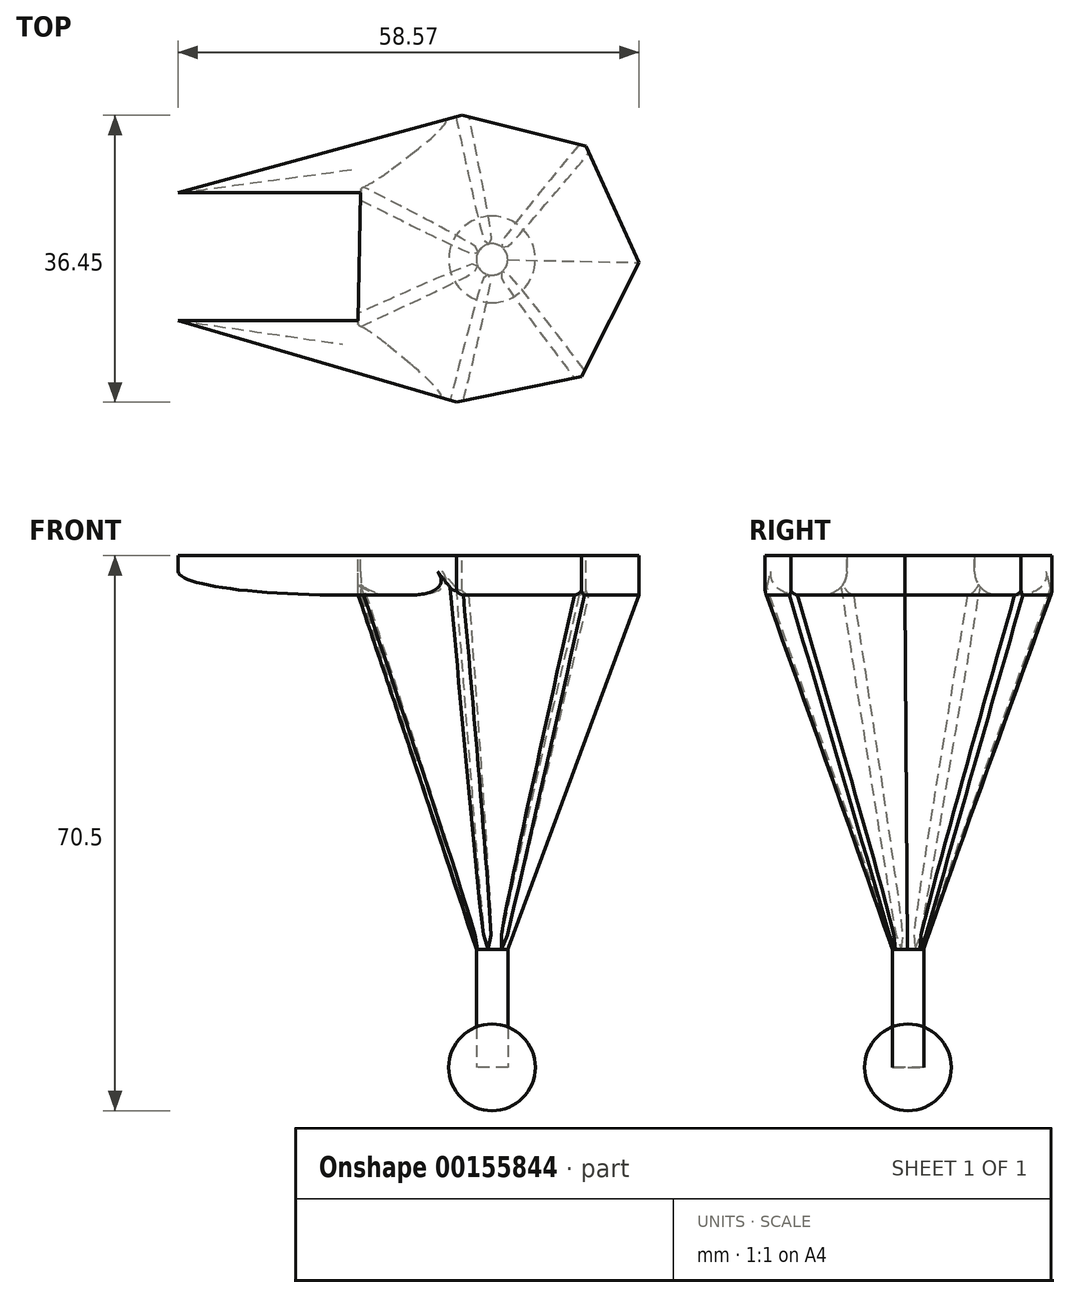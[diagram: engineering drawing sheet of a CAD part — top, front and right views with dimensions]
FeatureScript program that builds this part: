
annotation { "Feature Type Name" : "Feature", "Feature Type Description" : "" }
export const myFeature = defineFeature(function(context is Context, id is Id, definition is map)
    precondition{}
    {
        {
            var Q0;
            Q0=qCreatedBy(makeId("Top.planeOp"),FACE);
            var sketch = newSketch(context, id + "F0", { "sketchPlane" : qUnion([Q0])});
            skArc(sketch, "E0", {"start": v(-48.64, 0.62) * mm, "mid": v(-54.14, -4.88) * mm, "end": v(-48.64, -10.38) * mm});
            skLineSegment(sketch, "E1", {"start": v(-48.64, 0.62) * mm, "end": v(-48.64, -10.38) * mm});
            skSolve(sketch);
        }
        {
            var Q0;
            Q0=makeQuery(id+"F0.imprint","IMPRINT",FACE,{"disambiguationData":[TD([[makeQuery(id+"F0.imprint","IMPRINT",EDGE,{"derivedFrom":sQuery(id+"F0.wireOp",EDGE,"E0")}),1.0]])]});
            var Q1;
            Q1=sQuery(id+"F0.wireOp",EDGE,"E1");
            revolve(context, id + "F1", {"entities" : qUnion([Q0]), "axis" : qUnion([Q1]), "revolveType" : RevolveType.FULL});
        }
        {
            var Q0;
            Q0=qCreatedBy(makeId("Top.planeOp"),FACE);
            var sketch = newSketch(context, id + "F2", { "sketchPlane" : qUnion([Q0])});
            skPoint(sketch, "E2.0", {"position": v(-48.64, -4.88) * mm});
            skCircle(sketch, "E3", {"center": v(-48.64, -4.88) * mm, "radius": 2 * mm});
            skSolve(sketch);
        }
        {
            var Q0;
            Q0=makeQuery(id+"F2.imprint","IMPRINT",FACE,{"disambiguationData":[TD([[makeQuery(id+"F2.imprint","IMPRINT",EDGE,{"derivedFrom":sQuery(id+"F2.wireOp",EDGE,"E3")}),1.0]])]});
            extrude(context, id + "F3", {"entities" : qUnion([Q0]), "depth" : 15 * mm});
        }
        {
            var Q0;
            Q0=qCreatedBy(makeId("Top.planeOp"),FACE);
            cPlane(context, id + "F4", {"entities" : qUnion([Q0]), "cplaneType" : CPlaneType.OFFSET, "offset" : 60 * mm, "width" : 150 * mm, "height" : 150 * mm});
        }
        {
            var Q0;
            Q0=qCreatedBy(id+"F4.planeOp",FACE);
            var sketch = newSketch(context, id + "F5", { "sketchPlane" : qUnion([Q0])});
            skPoint(sketch, "E4.0", {"position": v(-48.64, -4.88) * mm});
            skCircle(sketch, "E5.cCircle", {"center": v(-48.64, -4.88) * mm, "radius": 16.84 * mm, "construction": true});
            skLineSegment(sketch, "E5.0", {"start": v(-37.3, -19.74) * mm, "end": v(-53.18, -23.02) * mm});
            skLineSegment(sketch, "E5.1", {"start": v(-53.18, -23.02) * mm, "end": v(-65.65, -12.64) * mm});
            skLineSegment(sketch, "E5.2", {"start": v(-65.65, -12.64) * mm, "end": v(-65.32, 3.58) * mm});
            skLineSegment(sketch, "E5.3", {"start": v(-65.32, 3.58) * mm, "end": v(-52.43, 13.43) * mm});
            skLineSegment(sketch, "E5.4", {"start": v(-52.43, 13.43) * mm, "end": v(-36.69, 9.5) * mm});
            skLineSegment(sketch, "E5.5", {"start": v(-36.69, 9.5) * mm, "end": v(-29.95, -5.27) * mm});
            skLineSegment(sketch, "E5.6", {"start": v(-29.95, -5.27) * mm, "end": v(-37.3, -19.74) * mm});
            skPoint(sketch, "E5.0.midPoint", {"position": v(-45.24, -21.38) * mm});
            skSolve(sketch);
        }
        {
            var Q0;
            Q0=makeQuery(id+"F3.opExtrude","CAP_FACE",FACE,{"disambiguationData":[OSD([sQuery(id+"F2.wireOp",EDGE,"E3")])],"isStart":false});
            var Q1;
            Q1=makeQuery(id+"F5.imprint","IMPRINT",FACE,{"disambiguationData":[TD([[makeQuery(id+"F5.imprint","IMPRINT",EDGE,{"derivedFrom":sQuery(id+"F5.wireOp",EDGE,"E5.0")}),-1.0]])]});
            loft(context, id + "F6", {"sheetProfilesArray" : [{ "sheetProfileEntities" : qUnion([Q0]) }, { "sheetProfileEntities" : qUnion([Q1]) }]});
        }
        {
            var Q0;
            Q0=makeQuery(id+"F6.opLoft","CAP_FACE",FACE,{"disambiguationData":[OSD([makeQuery(id+"F5.imprint","IMPRINT",FACE,{"disambiguationData":[TD([[makeQuery(id+"F5.imprint","IMPRINT",EDGE,{"derivedFrom":sQuery(id+"F5.wireOp",EDGE,"E5.0")}),-1.0]])]})])],"isStart":true});
            var sketch = newSketch(context, id + "F7", { "sketchPlane" : qUnion([Q0])});
            skLineSegment(sketch, "E6", {"start": v(-52.43, 13.43) * mm, "end": v(-88.52, 3.58) * mm});
            skLineSegment(sketch, "E7", {"start": v(-53.18, -23.02) * mm, "end": v(-88.52, -12.64) * mm});
            skLineSegment(sketch, "E8", {"start": v(-88.52, -12.64) * mm, "end": v(-65.65, -12.64) * mm});
            skLineSegment(sketch, "E9", {"start": v(-88.52, 3.58) * mm, "end": v(-65.32, 3.58) * mm});
            skSolve(sketch);
        }
        {
            var Q0;
            Q0=makeQuery(id+"F7.imprint","IMPRINT",FACE,{"disambiguationData":[TD([[makeQuery(id+"F7.imprint","IMPRINT",EDGE,{"derivedFrom":sQuery(id+"F7.wireOp",EDGE,"E6")}),1.0]])]});
            var Q1;
            {var subQ2=sQuery(id+"F5.wireOp",EDGE,"E5.1");var subQ3=sQuery(id+"F5.wireOp",EDGE,"E5.0");var subQ4=sQuery(id+"F5.wireOp",EDGE,"E5.6");Q1=makeQuery(id+"F7.imprint","IMPRINT",FACE,{"disambiguationData":[TD([[makeQuery(id+"F7.imprint","IMPRINT",EDGE,{"derivedFrom":makeQuery(id+"F6.opLoft","MID_CAP_EDGE",EDGE,{"disambiguationData":[OSD([subQ3,subQ2,subQ4])],"capPos":1.0})}),1.0]])]});}
            var Q2;
            Q2=makeQuery(id+"F7.imprint","IMPRINT",FACE,{"disambiguationData":[TD([[makeQuery(id+"F7.imprint","IMPRINT",EDGE,{"derivedFrom":sQuery(id+"F7.wireOp",EDGE,"E7")}),-1.0]])]});
            extrude(context, id + "F8", {"entities" : qUnion([Q0, Q1, Q2]), "operationType" : NewBodyOperationType.ADD, "depth" : 5 * mm});
        }
        {
            var Q0;
            Q0=makeQuery(id+"F8.opExtrude","CAP_EDGE",EDGE,{"disambiguationData":[OSD([sQuery(id+"F7.wireOp",EDGE,"E7")])],"isStart":true});
            var Q1;
            Q1=makeQuery(id+"F8.opExtrude","CAP_EDGE",EDGE,{"disambiguationData":[OSD([sQuery(id+"F7.wireOp",EDGE,"E8")])],"isStart":true});
            var Q2;
            Q2=makeQuery(id+"F8.opExtrude","CAP_EDGE",EDGE,{"disambiguationData":[OSD([sQuery(id+"F7.wireOp",EDGE,"E9")])],"isStart":true});
            var Q3;
            Q3=makeQuery(id+"F8.opExtrude","CAP_EDGE",EDGE,{"disambiguationData":[OSD([sQuery(id+"F7.wireOp",EDGE,"E6")])],"isStart":true});
            fillet(context, id + "F9", {"entities" : qUnion([Q0, Q1, Q2, Q3]), "radius" : 3 * mm, "tangentPropagation" : true, "allowEdgeOverflow" : false});
        }
        {
            var Q0;
            Q0=makeQuery(id+"F6.opLoft","SWEPT_EDGE",EDGE,{"disambiguationData":[OSD([sQuery(id+"F2.wireOp",EDGE,"E3"),sQuery(id+"F5.wireOp",EDGE,"E5.1"),sQuery(id+"F5.wireOp",EDGE,"E5.2"),sQuery(id+"F5.wireOp",EDGE,"E5.3")])]});
            var Q1;
            Q1=makeQuery(id+"F6.opLoft","SWEPT_EDGE",EDGE,{"disambiguationData":[OSD([sQuery(id+"F2.wireOp",EDGE,"E3"),sQuery(id+"F5.wireOp",EDGE,"E5.2"),sQuery(id+"F5.wireOp",EDGE,"E5.3"),sQuery(id+"F5.wireOp",EDGE,"E5.4")])]});
            var Q2;
            Q2=makeQuery(id+"F6.opLoft","SWEPT_EDGE",EDGE,{"disambiguationData":[OSD([sQuery(id+"F2.wireOp",EDGE,"E3"),sQuery(id+"F5.wireOp",EDGE,"E5.0"),sQuery(id+"F5.wireOp",EDGE,"E5.1"),sQuery(id+"F5.wireOp",EDGE,"E5.2")])]});
            var Q3;
            Q3=makeQuery(id+"F6.opLoft","SWEPT_EDGE",EDGE,{"disambiguationData":[OSD([sQuery(id+"F5.wireOp",EDGE,"E5.0"),sQuery(id+"F5.wireOp",EDGE,"E5.6")])]});
            var Q4;
            Q4=makeQuery(id+"F6.opLoft","SWEPT_EDGE",EDGE,{"disambiguationData":[OSD([sQuery(id+"F2.wireOp",EDGE,"E3"),sQuery(id+"F5.wireOp",EDGE,"E5.3"),sQuery(id+"F5.wireOp",EDGE,"E5.4"),sQuery(id+"F5.wireOp",EDGE,"E5.5")])]});
            var Q5;
            Q5=makeQuery(id+"F6.opLoft","SWEPT_EDGE",EDGE,{"disambiguationData":[OSD([sQuery(id+"F2.wireOp",EDGE,"E3"),sQuery(id+"F5.wireOp",EDGE,"E5.4"),sQuery(id+"F5.wireOp",EDGE,"E5.5"),sQuery(id+"F5.wireOp",EDGE,"E5.6")])]});
            var Q6;
            Q6=makeQuery(id+"F6.opLoft","SWEPT_EDGE",EDGE,{"disambiguationData":[OSD([sQuery(id+"F2.wireOp",EDGE,"E3"),sQuery(id+"F5.wireOp",EDGE,"E5.0"),sQuery(id+"F5.wireOp",EDGE,"E5.5"),sQuery(id+"F5.wireOp",EDGE,"E5.6")])]});
            fillet(context, id + "F10", {"entities" : qUnion([Q0, Q1, Q2, Q3, Q4, Q5, Q6]), "radius" : 2 * mm, "tangentPropagation" : true, "allowEdgeOverflow" : false});
        }
    });
